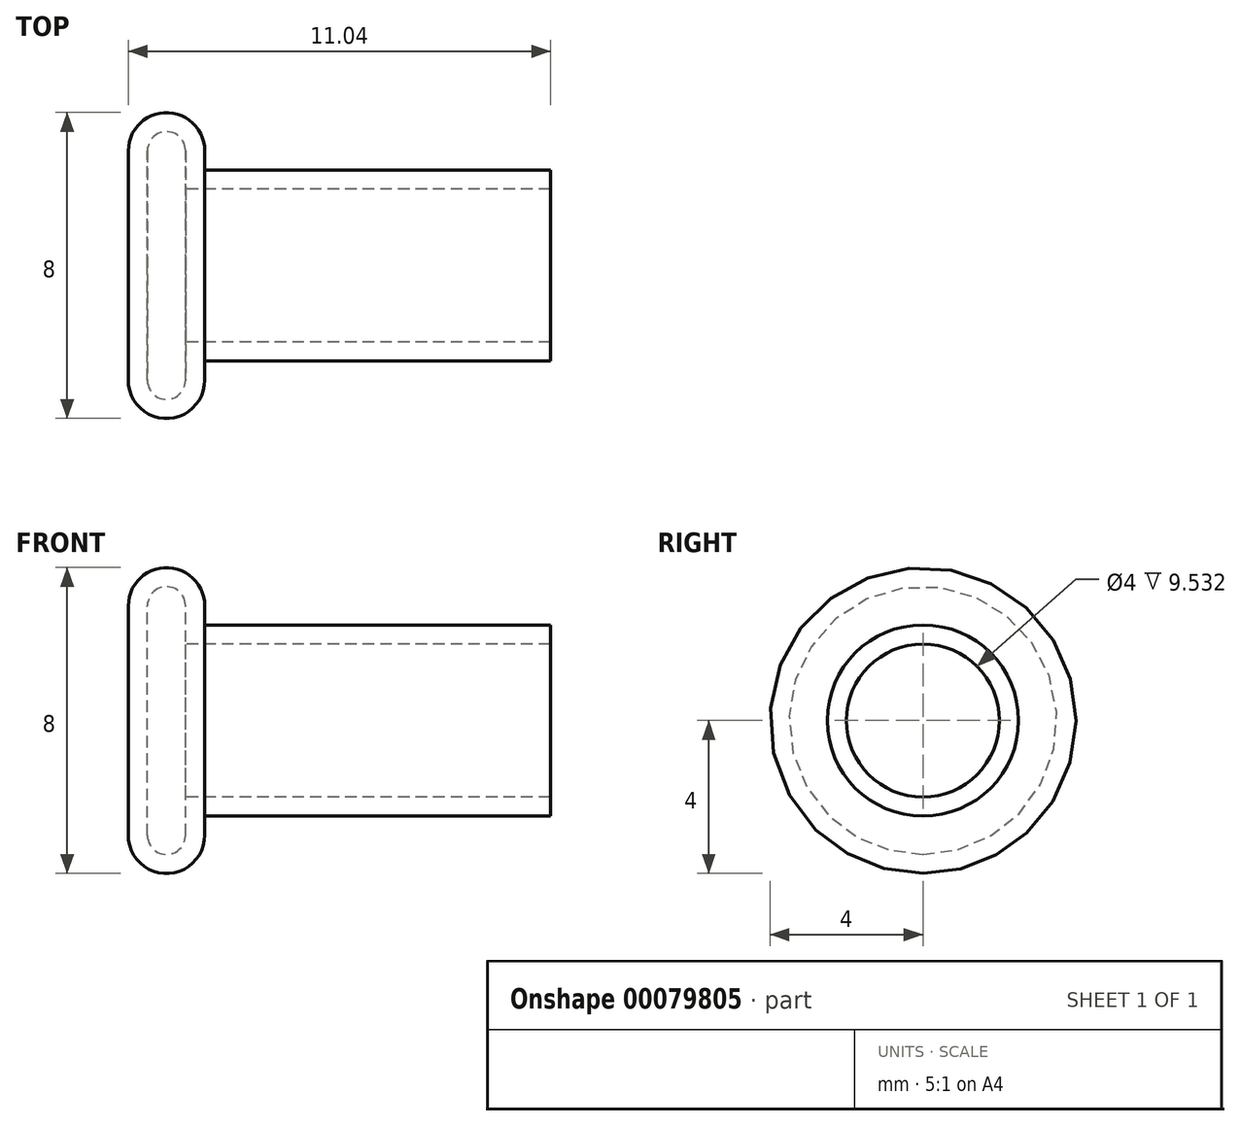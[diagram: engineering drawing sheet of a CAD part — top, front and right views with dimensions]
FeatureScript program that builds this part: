
annotation { "Feature Type Name" : "Feature", "Feature Type Description" : "" }
export const myFeature = defineFeature(function(context is Context, id is Id, definition is map)
    precondition{}
    {
        {
            var Q0;
            Q0=qCreatedBy(makeId("Front.planeOp"),FACE);
            var sketch = newSketch(context, id + "F0", { "sketchPlane" : qUnion([Q0])});
            skLineSegment(sketch, "E0", {"start": v(0, 0) * mm, "end": v(11, 0) * mm});
            skLineSegment(sketch, "E1", {"start": v(0, 0) * mm, "end": v(0, 4) * mm});
            skLineSegment(sketch, "E2", {"start": v(0, 4) * mm, "end": v(2, 4) * mm});
            skLineSegment(sketch, "E3", {"start": v(2, 4) * mm, "end": v(2, 2.5) * mm});
            skLineSegment(sketch, "E4", {"start": v(2, 2.5) * mm, "end": v(11.04, 2.5) * mm});
            skLineSegment(sketch, "E5", {"start": v(11.04, 2.5) * mm, "end": v(11, 0) * mm});
            skSolve(sketch);
        }
        {
            var Q0;
            Q0=qCreatedBy(makeId("Front.planeOp"),FACE);
            var sketch = newSketch(context, id + "F1", { "sketchPlane" : qUnion([Q0])});
            skLineSegment(sketch, "E6", {"start": v(-34.73, 0) * mm, "end": v(48.19, 0) * mm, "construction": true});
            skSolve(sketch);
        }
        {
            var Q0;
            Q0 = qSketchRegion(id + "F0", true);
            var Q1;
            Q1 = qBodyType(qCreatedBy(id + "F1" ,EDGE), BodyType.WIRE);
            revolve(context, id + "F2", {"entities" : qUnion([Q0]), "axis" : qUnion([Q1]), "revolveType" : RevolveType.FULL});
        }
        {
            var Q0;
            Q0=makeQuery(id+"F2.opRevolve","SWEPT_EDGE",EDGE,{"disambiguationData":[OSD([sQuery(id+"F0.wireOp",EDGE,"E2"),sQuery(id+"F0.wireOp",EDGE,"E3")])]});
            var Q1;
            Q1=makeQuery(id+"F2.opRevolve","SWEPT_EDGE",EDGE,{"disambiguationData":[OSD([sQuery(id+"F0.wireOp",EDGE,"E1"),sQuery(id+"F0.wireOp",EDGE,"E2")])]});
            fillet(context, id + "F4", {"entities" : qUnion([Q0, Q1]), "radius" : 1 * mm, "tangentPropagation" : true, "allowEdgeOverflow" : false});
        }
        {
            var Q0;
            Q0=makeQuery(id+"F2.opRevolve","SWEPT_FACE",FACE,{"disambiguationData":[OSD([sQuery(id+"F0.wireOp",EDGE,"E5")])]});
            shell(context, id + "F3", {"entities" : qUnion([Q0]), "thickness" : 0.5 * mm});
        }
    });
